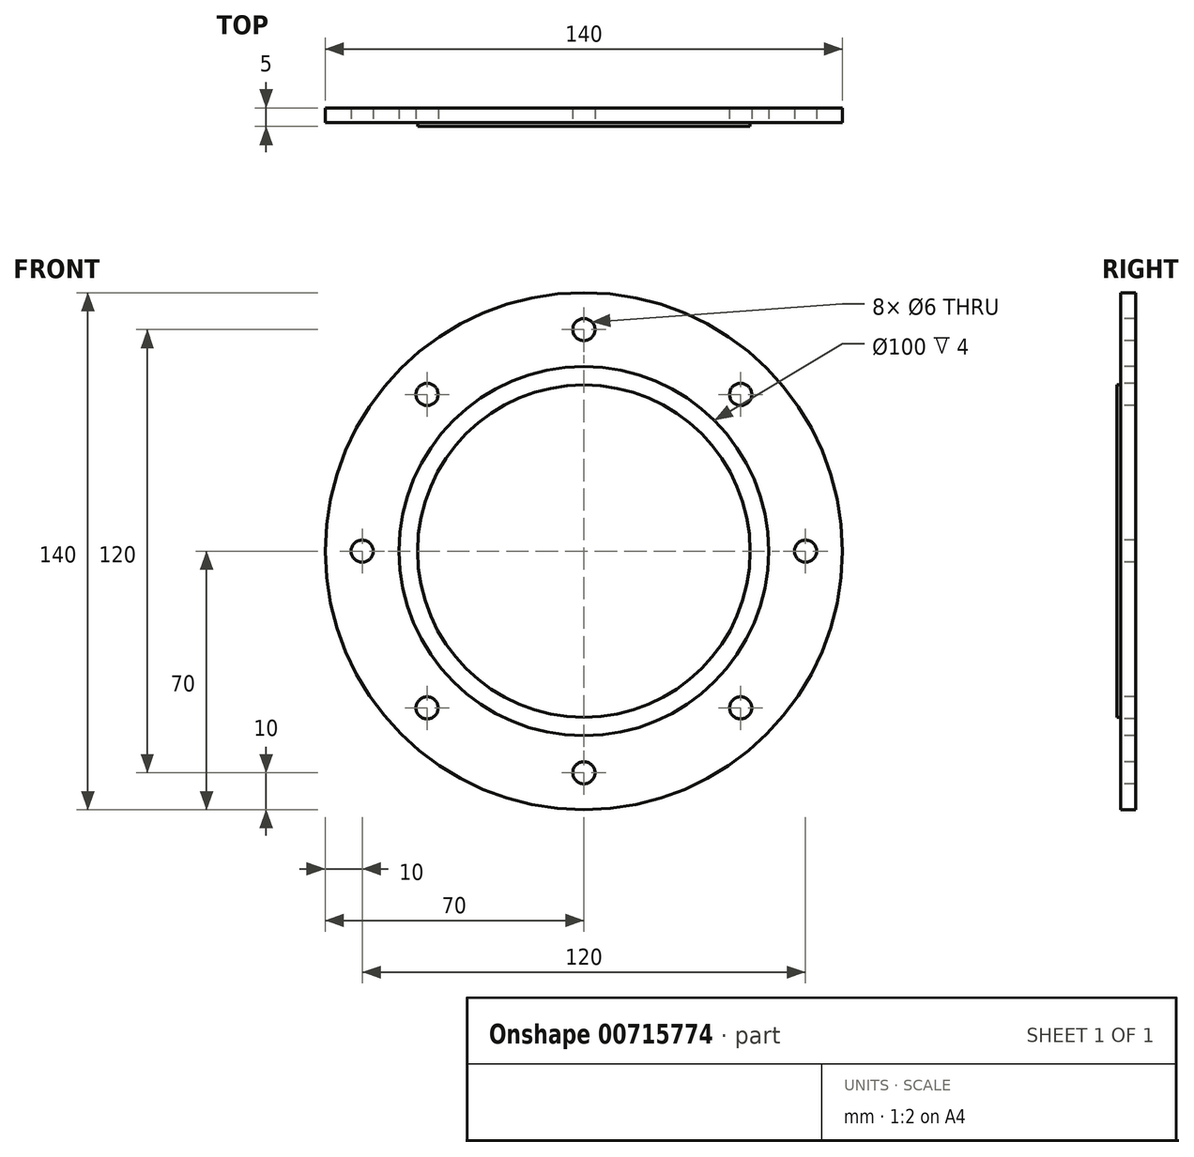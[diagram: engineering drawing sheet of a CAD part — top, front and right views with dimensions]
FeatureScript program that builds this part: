
annotation { "Feature Type Name" : "Feature", "Feature Type Description" : "" }
export const myFeature = defineFeature(function(context is Context, id is Id, definition is map)
    precondition{}
    {
        {
            var Q0;
            Q0=qCreatedBy(makeId("Front.planeOp"),FACE);
            var sketch = newSketch(context, id + "F0", { "sketchPlane" : qUnion([Q0])});
            skCircle(sketch, "E0", {"center": v(0, 0) * mm, "radius": 50 * mm});
            skCircle(sketch, "E1", {"center": v(0, 0) * mm, "radius": 70 * mm});
            skCircle(sketch, "E2", {"center": v(0, 60) * mm, "radius": 3 * mm});
            skCircle(sketch, "E3", {"center": v(0, 60) * mm, "radius": 5.5 * mm});
            skCircle(sketch, "E4.1.0", {"center": v(-42.43, 42.43) * mm, "radius": 5.5 * mm});
            skCircle(sketch, "E4.1.1", {"center": v(-42.43, 42.43) * mm, "radius": 3 * mm});
            skCircle(sketch, "E4.2.0", {"center": v(-60, 0) * mm, "radius": 5.5 * mm});
            skCircle(sketch, "E4.2.1", {"center": v(-60, 0) * mm, "radius": 3 * mm});
            skCircle(sketch, "E4.3.0", {"center": v(-42.43, -42.43) * mm, "radius": 5.5 * mm});
            skCircle(sketch, "E4.3.1", {"center": v(-42.43, -42.43) * mm, "radius": 3 * mm});
            skCircle(sketch, "E4.4.0", {"center": v(0, -60) * mm, "radius": 5.5 * mm});
            skCircle(sketch, "E4.4.1", {"center": v(0, -60) * mm, "radius": 3 * mm});
            skCircle(sketch, "E4.5.0", {"center": v(42.43, -42.43) * mm, "radius": 5.5 * mm});
            skCircle(sketch, "E4.5.1", {"center": v(42.43, -42.43) * mm, "radius": 3 * mm});
            skCircle(sketch, "E4.6.0", {"center": v(60, 0) * mm, "radius": 5.5 * mm});
            skCircle(sketch, "E4.6.1", {"center": v(60, 0) * mm, "radius": 3 * mm});
            skCircle(sketch, "E4.7.0", {"center": v(42.43, 42.43) * mm, "radius": 5.5 * mm});
            skCircle(sketch, "E4.7.1", {"center": v(42.43, 42.43) * mm, "radius": 3 * mm});
            skSolve(sketch);
        }
        {
            var Q0;
            Q0=makeQuery(id+"F0.imprint","IMPRINT",FACE,{"disambiguationData":[TD([[makeQuery(id+"F0.imprint","IMPRINT",EDGE,{"derivedFrom":sQuery(id+"F0.wireOp",EDGE,"E0")}),-1.0]])]});
            var Q1;
            Q1=makeQuery(id+"F0.imprint","IMPRINT",FACE,{"disambiguationData":[TD([[makeQuery(id+"F0.imprint","IMPRINT",EDGE,{"derivedFrom":sQuery(id+"F0.wireOp",EDGE,"E4.1.0")}),1.0]])]});
            var Q2;
            Q2=makeQuery(id+"F0.imprint","IMPRINT",FACE,{"disambiguationData":[TD([[makeQuery(id+"F0.imprint","IMPRINT",EDGE,{"derivedFrom":sQuery(id+"F0.wireOp",EDGE,"E4.2.0")}),1.0]])]});
            var Q3;
            Q3=makeQuery(id+"F0.imprint","IMPRINT",FACE,{"disambiguationData":[TD([[makeQuery(id+"F0.imprint","IMPRINT",EDGE,{"derivedFrom":sQuery(id+"F0.wireOp",EDGE,"E2")}),-1.0]])]});
            var Q4;
            Q4=makeQuery(id+"F0.imprint","IMPRINT",FACE,{"disambiguationData":[TD([[makeQuery(id+"F0.imprint","IMPRINT",EDGE,{"derivedFrom":sQuery(id+"F0.wireOp",EDGE,"E4.7.0")}),1.0]])]});
            var Q5;
            Q5=makeQuery(id+"F0.imprint","IMPRINT",FACE,{"disambiguationData":[TD([[makeQuery(id+"F0.imprint","IMPRINT",EDGE,{"derivedFrom":sQuery(id+"F0.wireOp",EDGE,"E4.6.0")}),1.0]])]});
            var Q6;
            Q6=makeQuery(id+"F0.imprint","IMPRINT",FACE,{"disambiguationData":[TD([[makeQuery(id+"F0.imprint","IMPRINT",EDGE,{"derivedFrom":sQuery(id+"F0.wireOp",EDGE,"E4.5.0")}),1.0]])]});
            var Q7;
            Q7=makeQuery(id+"F0.imprint","IMPRINT",FACE,{"disambiguationData":[TD([[makeQuery(id+"F0.imprint","IMPRINT",EDGE,{"derivedFrom":sQuery(id+"F0.wireOp",EDGE,"E4.4.0")}),1.0]])]});
            var Q8;
            Q8=makeQuery(id+"F0.imprint","IMPRINT",FACE,{"disambiguationData":[TD([[makeQuery(id+"F0.imprint","IMPRINT",EDGE,{"derivedFrom":sQuery(id+"F0.wireOp",EDGE,"E4.3.0")}),1.0]])]});
            extrude(context, id + "F1", {"entities" : qUnion([Q0, Q1, Q2, Q3, Q4, Q5, Q6, Q7, Q8]), "depth" : -4 * mm, "offsetDistance" : 25 * mm});
        }
        {
            var Q0;
            Q0=qCreatedBy(makeId("Front.planeOp"),FACE);
            var sketch = newSketch(context, id + "F2", { "sketchPlane" : qUnion([Q0])});
            skCircle(sketch, "E5", {"center": v(0, 0) * mm, "radius": 45 * mm});
            skSolve(sketch);
        }
        {
            var Q0;
            Q0=makeQuery(id+"F2.imprint","IMPRINT",FACE,{"disambiguationData":[TD([[makeQuery(id+"F2.imprint","IMPRINT",EDGE,{"derivedFrom":sQuery(id+"F2.wireOp",EDGE,"E5")}),1.0]])]});
            extrude(context, id + "F3", {"entities" : qUnion([Q0]), "depth" : 1 * mm, "offsetDistance" : 25 * mm});
        }
    });
